FCSTD DOCUMENT  (FreeCAD 0.20R29410 (Git))
Label: simbologia-abnt
License: All rights reserved
objects: Part::Part2DObjectPython×43, App::FeaturePython×17, App::DocumentObjectGroup×12, Part::Mirroring×4, Part::FeaturePython×1
note: 47 computed .brp shape members not serialized (recipe doc carries the construction recipe); baked Part::Feature solids carry a one-line shape summary decoded from their .brp

FEATURE [Part::Part2DObjectPython] Line  # Draft 2D object (typed FeaturePython)
  Area = 0
  ChamferSize = 0
  Closed = true
  End = (0,7.75736,0)
  FilletRadius = 0
  Length = 7.75736
  MakeFace = true
  Points = (2) [(0,0,0),(0,7.75736,0)]
  Start = (0,0,0)
  Subdivisions = 0
FEATURE [Part::Part2DObjectPython] Line001  # Draft 2D object (typed FeaturePython)
  Area = 0
  ChamferSize = 0
  Closed = true
  End = (5,7.75736,0)
  FilletRadius = 0
  Length = 7.75736
  MakeFace = true
  Placement = pos=(5,0,0) rot=(0,0,1;0rad)
  Points = (2) [(0,0,0),(0,7.75736,0)]
  Start = (5,0,0)
  Subdivisions = 0
FEATURE [Part::Part2DObjectPython] Line003  # Draft 2D object (typed FeaturePython)
  Area = 0
  ChamferSize = 0
  Closed = false
  End = (6.74264,7.75736,0)
  FilletRadius = 0
  Length = 6
  MakeFace = true
  Placement = pos=(2.5,12,0) rot=(0,0,1;0.785398rad)
  Points = (2) [(0,0,0),(1.77636e-15,-6,0)]
  Start = (2.5,12,0)
  Subdivisions = 0
FEATURE [Part::Mirroring] mirror  label="Line003 (espelhado) "
  Base = (2.5,5.47945,0)
  Normal = (1,0,0)
  Source = -> Line003
FEATURE [Part::Part2DObjectPython] Line004  # Draft 2D object (typed FeaturePython)
  Area = 0
  ChamferSize = 0
  Closed = false
  End = (4e-16,7.75736,0)
  FilletRadius = 0
  Length = 1.74264
  MakeFace = true
  Placement = pos=(-1.74264,7.75736,0) rot=(0,0,1;0rad)
  Points = (2) [(0,0,0),(1.74264,0,0)]
  Start = (-1.74264,7.75736,0)
  Subdivisions = 0
FEATURE [Part::Part2DObjectPython] Line005  # Draft 2D object (typed FeaturePython)
  Area = 0
  ChamferSize = 0
  Closed = false
  End = (5,7.75736,0)
  FilletRadius = 0
  Length = 1.74264
  MakeFace = true
  Placement = pos=(6.74264,7.75736,0) rot=(0,0,1;0rad)
  Points = (2) [(0,0,0),(-1.74264,0,0)]
  Start = (6.74264,7.75736,0)
  Subdivisions = 0
FEATURE [Part::Part2DObjectPython] Line006  # Draft 2D object (typed FeaturePython)
  Area = 0
  ChamferSize = 0
  Closed = false
  End = (5,0,0)
  FilletRadius = 0
  Length = 5
  MakeFace = true
  Points = (2) [(0,0,0),(5,0,0)]
  Start = (0,0,0)
  Subdivisions = 0
FEATURE [App::FeaturePython] Text  label="ENTRADA"  # WARN: FeaturePython — macro-defined, semantics opaque (R4)
  Placement = pos=(-4.70483,-2.70715,0) rot=(0,0,1;0rad)
  Text = ENTRADA
FEATURE [App::DocumentObjectGroup] Group  label="simbologia-entrada"
  Group = -> [Line,Line001,mirror,Line004,Line005,Line006,Text]
FEATURE [Part::Part2DObjectPython] Line007  # Draft 2D object (typed FeaturePython)
  Area = 0
  ChamferSize = 0
  Closed = false
  End = (35.2588,-0.0306032,0)
  FilletRadius = 0
  Length = 12
  MakeFace = true
  Placement = pos=(23.2588,-0.0306032,0) rot=(0,0,1;0rad)
  Points = (2) [(0,0,0),(12,0,0)]
  Start = (23.2588,-0.0306032,0)
  Subdivisions = 0
FEATURE [Part::Part2DObjectPython] Line009  # Draft 2D object (typed FeaturePython)
  Area = 0
  ChamferSize = 0
  Closed = false
  End = (23.2588,-0.0306032,0)
  FilletRadius = 0
  Length = 8.48528
  MakeFace = true
  Placement = pos=(23.2588,-0.0306032,0) rot=(0,0,1;0.785398rad)
  Points = (2) [(7.10543e-15,-8.48528,0),(0,0,0)]
  Start = (29.2588,-6.0306,0)
  Subdivisions = 0
FEATURE [Part::Mirroring] mirror001  label="Line009 (espelhado) "
  Base = (29.2588,-0.0306032,0)
  Normal = (-1,0,0)
  Source = -> Line009
FEATURE [App::FeaturePython] Text001  label="INCLINAÇÃO"  # WARN: FeaturePython — macro-defined, semantics opaque (R4)
  Placement = pos=(26.5157,0.363858,0) rot=(0,0,1;0rad)
  Text = xx %
FEATURE [App::DocumentObjectGroup] Group001  label="simbologia-inclinação-telhado"
  Group = -> [Line007,mirror001,Text001]
FEATURE [Part::Part2DObjectPython] Circle  # Draft 2D object (typed FeaturePython)
  Area = 0
  FirstAngle = 0
  LastAngle = 0
  MakeFace = false
  Placement = pos=(46.9739,-0.162971,0) rot=(0,0,1;0rad)
  Radius = 6
FEATURE [Part::Part2DObjectPython] Line010  # Draft 2D object (typed FeaturePython)
  Area = 0
  ChamferSize = 0
  Closed = false
  End = (52.9739,-0.162971,0)
  FilletRadius = 0
  Length = 12
  MakeFace = true
  Placement = pos=(40.9739,-0.162971,0) rot=(0,0,1;0rad)
  Points = (2) [(0,0,0),(12,-7.21645e-16,0)]
  Start = (40.9739,-0.162971,0)
  Subdivisions = 0
FEATURE [Part::Part2DObjectPython] Line011  # Draft 2D object (typed FeaturePython)
  Area = 0
  ChamferSize = 0
  Closed = false
  End = (40.9739,-0.162971,0)
  FilletRadius = 0
  Length = 3
  MakeFace = true
  Placement = pos=(37.9739,-0.162971,0) rot=(0,0,1;0rad)
  Points = (2) [(0,0,0),(3,0,0)]
  Start = (37.9739,-0.162971,0)
  Subdivisions = 0
FEATURE [Part::Part2DObjectPython] Line013  # Draft 2D object (typed FeaturePython)
  Area = 0
  ChamferSize = 0
  Closed = false
  End = (55.9739,-0.162971,0)
  FilletRadius = 0
  Length = 3
  MakeFace = true
  Placement = pos=(52.9739,-0.162971,0) rot=(0,0,1;0rad)
  Points = (2) [(0,0,0),(3,0,0)]
  Start = (52.9739,-0.162971,0)
  Subdivisions = 0
FEATURE [Part::Part2DObjectPython] Line014  # Draft 2D object (typed FeaturePython)
  Area = 0
  ChamferSize = 0
  Closed = false
  End = (37.9739,-0.162971,0)
  FilletRadius = 0
  Length = 12.7279
  MakeFace = true
  Placement = pos=(37.9739,-0.162971,0) rot=(0,0,1;0rad)
  Points = (2) [(9,9,0),(0,-7.21645e-16,0)]
  Start = (46.9739,8.83703,0)
  Subdivisions = 0
FEATURE [Part::Mirroring] mirror002  label="Line014 (espelhado) "
  Base = (46.9739,13.4063,0)
  Normal = (-1,0,0)
  Source = -> Line014
FEATURE [App::FeaturePython] Text002  label="DESENHO-NUM"  # WARN: FeaturePython — macro-defined, semantics opaque (R4)
  Placement = pos=(45.2497,1.29047,0) rot=(0,0,1;0rad)
  Text = xx
FEATURE [App::FeaturePython] Text003  label="PRANCHA-NUM"  # WARN: FeaturePython — macro-defined, semantics opaque (R4)
  Placement = pos=(45.7357,-2.81605,0) rot=(0,0,1;0rad)
  Text = xx
FEATURE [App::DocumentObjectGroup] Group002  label="simbologia-elev-corte-fachada-vista"
  Group = -> [Circle,Line010,Line011,Line013,mirror002,Text002,Text003]
FEATURE [Part::Part2DObjectPython] Circle001  # Draft 2D object (typed FeaturePython)
  Area = 0
  FirstAngle = 0
  LastAngle = 0
  MakeFace = false
  Placement = pos=(72.2369,-0.0494289,0) rot=(0,0,1;0rad)
  Radius = 5
FEATURE [Part::Part2DObjectPython] Line017  # Draft 2D object (typed FeaturePython)
  Area = 0
  ChamferSize = 0
  Closed = false
  End = (92.2369,-0.0494289,0)
  FilletRadius = 0
  Length = 30
  MakeFace = true
  Placement = pos=(62.2369,-0.0494289,0) rot=(0,0,1;0rad)
  Points = (2) [(0,0,0),(30,0,0)]
  Start = (62.2369,-0.0494289,0)
  Subdivisions = 0
FEATURE [Part::Part2DObjectPython] Line018  # Draft 2D object (typed FeaturePython)
  Area = 0
  ChamferSize = 0
  Closed = false
  End = (71.9166,9.95057,0)
  FilletRadius = 0
  Length = 20
  MakeFace = true
  Placement = pos=(71.9166,-10.0494,0) rot=(0,0,1;0rad)
  Points = (2) [(0,0,0),(0,20,0)]
  Start = (71.9166,-10.0494,0)
  Subdivisions = 0
FEATURE [App::FeaturePython] Text004  label="NÍVEL-PLANTA"  # WARN: FeaturePython — macro-defined, semantics opaque (R4)
  Placement = pos=(77.4379,1.13189,0) rot=(0,0,1;0rad)
  Text = + XX,XX 
FEATURE [App::DocumentObjectGroup] Group003  label="simbologia-nível-planta"
  Group = -> [Circle001,Line017,Line018,Text004]
FEATURE [Part::Part2DObjectPython] Line019  # Draft 2D object (typed FeaturePython)
  Area = 0
  ChamferSize = 0
  Closed = false
  End = (111.872,1.47777,0)
  FilletRadius = 0
  Length = 2.5
  MakeFace = true
  Placement = pos=(113.64,-0.29,0) rot=(0,0,1;0.785398rad)
  Points = (2) [(0,0,0),(-1.42109e-14,2.5,0)]
  Start = (113.64,-0.29,0)
  Subdivisions = 0
FEATURE [Part::Mirroring] mirror003  label="Line019 (espelhado) "
  Base = (113.64,-0.29,0)
  Normal = (1,0,0)
  Source = -> Line019
FEATURE [Part::Part2DObjectPython] Line020  # Draft 2D object (typed FeaturePython)
  Area = 0
  ChamferSize = 0
  Closed = false
  End = (115.408,1.47777,0)
  FilletRadius = 0
  Length = 3.53553
  MakeFace = true
  Placement = pos=(111.872,1.47777,0) rot=(0,0,1;0rad)
  Points = (2) [(0,0,0),(3.53553,1.42109e-14,0)]
  Start = (111.872,1.47777,0)
  Subdivisions = 0
FEATURE [Part::Part2DObjectPython] Line021  # Draft 2D object (typed FeaturePython)
  Area = 0
  ChamferSize = 0
  Closed = false
  End = (115.408,1.47777,0)
  FilletRadius = 0
  Length = 3.53553
  MakeFace = true
  Placement = pos=(111.872,1.47777,0) rot=(0,0,1;0rad)
  Points = (2) [(0,0,0),(3.53553,1.42109e-14,0)]
  Start = (111.872,1.47777,0)
  Subdivisions = 0
FEATURE [Part::Part2DObjectPython] Line022  # Draft 2D object (typed FeaturePython)
  Area = 0
  ChamferSize = 0
  Closed = false
  End = (113.64,9.71,0)
  FilletRadius = 0
  Length = 10
  MakeFace = true
  Placement = pos=(113.64,-0.29,0) rot=(0,0,1;0rad)
  Points = (2) [(0,0,0),(0,10,0)]
  Start = (113.64,-0.29,0)
  Subdivisions = 0
FEATURE [App::FeaturePython] Text005  label="NÍVEL-CORTE"  # WARN: FeaturePython — macro-defined, semantics opaque (R4)
  Placement = pos=(114.511,5.46916,0) rot=(0,0,1;0rad)
  Text = + XX,XX  (X.X)
FEATURE [Part::Part2DObjectPython] Line026  # Draft 2D object (typed FeaturePython)
  Area = 0
  ChamferSize = 0
  Closed = false
  End = (131.687,4.71,0)
  FilletRadius = 0
  Length = 21.7968
  MakeFace = true
  Placement = pos=(109.89,4.71,0) rot=(0,0,1;0rad)
  Points = (2) [(0,0,0),(21.7968,0,0)]
  Start = (109.89,4.71,0)
  Subdivisions = 0
FEATURE [App::DocumentObjectGroup] Group004  label="simbologia-nível-corte"
  Group = -> [mirror003,Line020,Line021,Line022,Text005,Line026]
FEATURE [Part::Part2DObjectPython] Circle003  # Draft 2D object (typed FeaturePython)
  Area = 0
  FirstAngle = 0
  LastAngle = 0
  MakeFace = false
  Placement = pos=(190.551,-0.0194988,0) rot=(0,0,1;0rad)
  Radius = 6
FEATURE [Part::Part2DObjectPython] Line028  # Draft 2D object (typed FeaturePython)
  Area = 0
  ChamferSize = 0
  Closed = false
  End = (250,-0.02,0)
  FilletRadius = 0
  Length = 53.4486
  MakeFace = true
  Placement = pos=(196.551,-0.0194988,0) rot=(0,0,1;0rad)
  Points = (2) [(0,0,0),(53.4486,-0.000501236,0)]
  Start = (196.551,-0.0194988,0)
  Subdivisions = 0
FEATURE [App::FeaturePython] Text008  label="TITULO-DESENHO"  # WARN: FeaturePython — macro-defined, semantics opaque (R4)
  Placement = pos=(196.849,0.792427,0) rot=(0,0,1;0rad)
  Text = TITULO DO DESENHO
FEATURE [App::FeaturePython] Text009  label="NUM-DESENHO"  # WARN: FeaturePython — macro-defined, semantics opaque (R4)
  Placement = pos=(189.054,-1.69787,0) rot=(0,0,1;0rad)
  Text = X
FEATURE [App::FeaturePython] Text010  label="ESCALA-DESENHO"  # WARN: FeaturePython — macro-defined, semantics opaque (R4)
  Placement = pos=(196.849,-3.27118,0) rot=(0,0,1;0rad)
  Text = ESCALA
FEATURE [App::DocumentObjectGroup] Group006  label="simbologia-titulo-prancha"
  Group = -> [Circle003,Line028,Text008,Text009,Text010]
FEATURE [Part::Part2DObjectPython] Circle004  # Draft 2D object (typed FeaturePython)
  Area = 0
  FirstAngle = 0
  LastAngle = 0
  MakeFace = false
  Placement = pos=(273.103,0.232803,0) rot=(0,0,1;0rad)
  Radius = 3.5
FEATURE [App::FeaturePython] Text011  label="SIGLA-ESQUADRIAS"  # WARN: FeaturePython — macro-defined, semantics opaque (R4)
  Placement = pos=(271.713,-0.498117,0) rot=(0,0,1;0rad)
  Text = Xn
FEATURE [Part::Part2DObjectPython] Circle005  # Draft 2D object (typed FeaturePython)
  Area = 0
  FirstAngle = 0
  LastAngle = 0
  MakeFace = false
  Placement = pos=(273.418,11.7931,0) rot=(0,0,1;0rad)
  Radius = 3.5
FEATURE [App::FeaturePython] Text012  label="SIGLA-ESQUADRIAS001"  # WARN: FeaturePython — macro-defined, semantics opaque (R4)
  Placement = pos=(272.029,11.0621,0) rot=(0,0,1;0rad)
  Text = Xn
FEATURE [Part::Part2DObjectPython] Circle006  # Draft 2D object (typed FeaturePython)
  Area = 0
  FirstAngle = 0
  LastAngle = 0
  MakeFace = false
  Placement = pos=(273.418,23.0764,0) rot=(0,0,1;0rad)
  Radius = 3.5
FEATURE [App::FeaturePython] Text013  label="SIGLA-ESQUADRIAS002"  # WARN: FeaturePython — macro-defined, semantics opaque (R4)
  Placement = pos=(272.029,22.3455,0) rot=(0,0,1;0rad)
  Text = Xn
FEATURE [App::FeaturePython] Text014  label="LARGxALT"  # WARN: FeaturePython — macro-defined, semantics opaque (R4)
  Placement = pos=(277.408,23.7992,0) rot=(0,0,1;0rad)
  Text = X,X x X,X
FEATURE [App::FeaturePython] Text015  label="PEITORIL"  # WARN: FeaturePython — macro-defined, semantics opaque (R4)
  Placement = pos=(280.577,20.7534,0) rot=(0,0,1;0rad)
  Text = X,X
FEATURE [Part::Part2DObjectPython] Line031  # Draft 2D object (typed FeaturePython)
  Area = 0
  ChamferSize = 0
  Closed = false
  End = (288.532,23.0764,0)
  FilletRadius = 0
  Length = 11.6135
  MakeFace = true
  Placement = pos=(276.918,23.0764,0) rot=(0,0,1;0rad)
  Points = (2) [(0,0,0),(11.6135,0,0)]
  Start = (276.918,23.0764,0)
  Subdivisions = 0
FEATURE [Part::Part2DObjectPython] Line032  # Draft 2D object (typed FeaturePython)
  Area = 0
  ChamferSize = 0
  Closed = false
  End = (288.532,11.7931,0)
  FilletRadius = 0
  Length = 11.6135
  MakeFace = true
  Placement = pos=(276.918,11.7931,0) rot=(0,0,1;0rad)
  Points = (2) [(0,0,0),(11.6135,0,0)]
  Start = (276.918,11.7931,0)
  Subdivisions = 0
FEATURE [App::FeaturePython] Text016  label="LARGxALT001"  # WARN: FeaturePython — macro-defined, semantics opaque (R4)
  Placement = pos=(277.408,12.5158,0) rot=(0,0,1;0rad)
  Text = X,X x X,X
FEATURE [App::DocumentObjectGroup] Group007  label="simbologia-esquadrias-medidas"
  Group = -> [Circle004,Text011,Circle005,Text012,Circle006,Text013,Text014,Text015,Line031,Line032,Text016]
FEATURE [Part::Part2DObjectPython] Line027  # Draft 2D object (typed FeaturePython)
  Area = 0
  ChamferSize = 0
  Closed = false
  End = (169.147,0.17771,0)
  FilletRadius = 0
  Length = 12
  MakeFace = true
  Placement = pos=(157.147,0.17771,0) rot=(0,0,1;0rad)
  Points = (2) [(0,0,0),(12,-7.21645e-16,0)]
  Start = (157.147,0.17771,0)
  Subdivisions = 0
FEATURE [App::FeaturePython] Text007  label="DESENHO-NUM001"  # WARN: FeaturePython — macro-defined, semantics opaque (R4)
  Placement = pos=(161.423,1.61442,0) rot=(0,0,1;0rad)
  Text = xx
FEATURE [App::FeaturePython] Text006  label="PRANCHA-NUM001"  # WARN: FeaturePython — macro-defined, semantics opaque (R4)
  Placement = pos=(161.909,-2.4921,0) rot=(0,0,1;0rad)
  Text = xx
FEATURE [Part::Part2DObjectPython] Circle002  # Draft 2D object (typed FeaturePython)
  Area = 0
  FirstAngle = 0
  LastAngle = 0
  MakeFace = false
  Placement = pos=(163.147,0.17771,0) rot=(0,0,1;0rad)
  Radius = 6
FEATURE [App::DocumentObjectGroup] Group005  label="simbologia-detalhes-e-ampliações"
  Group = -> [Circle002,Text006,Text007,Line027]
FEATURE [Part::Part2DObjectPython] Rectangle  # Draft 2D object (typed FeaturePython)
  Area = 0
  ChamferSize = 0
  Columns = 1
  FilletRadius = 0
  Height = 5
  Length = 5
  MakeFace = false
  Placement = pos=(-0.647244,30.44,0) rot=(0,0,1;0rad)
  Rows = 1
FEATURE [Part::Part2DObjectPython] Line033  # Draft 2D object (typed FeaturePython)
  Area = 0
  ChamferSize = 0
  Closed = false
  End = (9.35276,30.44,0)
  FilletRadius = 0
  Length = 5
  MakeFace = true
  Placement = pos=(4.35276,30.44,0) rot=(0,0,1;0rad)
  Points = (2) [(0,0,0),(5,0,0)]
  Start = (4.35276,30.44,0)
  Subdivisions = 0
FEATURE [Part::Part2DObjectPython] Circle007  # Draft 2D object (typed FeaturePython)
  Area = 0
  FirstAngle = 0
  LastAngle = 0
  MakeFace = false
  Placement = pos=(11.9208,32.94,0) rot=(0,0,1;0rad)
  Radius = 3
FEATURE [Part::Part2DObjectPython] Wire  # Draft 2D object (typed FeaturePython)
  Area = 0
  ChamferSize = 0
  Closed = false
  End = (9.35276,30.44,0)
  FilletRadius = 0
  Length = 10.4193
  MakeFace = true
  Placement = pos=(4.35276,30.44,0) rot=(0,0,1;0rad)
  Points = (3) [(0,0,0),(2.5,4.5706,0),(5,0,0)]
  Start = (4.35276,30.44,0)
  Subdivisions = 0
FEATURE [App::DocumentObjectGroup] Group008  label="simbologia-revestimentos"
  Group = -> [Rectangle,Line033,Circle007,Wire]
FEATURE [Part::Part2DObjectPython] Rectangle001  # Draft 2D object (typed FeaturePython)
  Area = 0
  ChamferSize = 0
  Columns = 1
  FilletRadius = 0
  Height = 26.2006
  Length = 77.4526
  MakeFace = false
  Placement = pos=(304.633,0.159356,0) rot=(0,0,1;0rad)
  Rows = 1
FEATURE [Part::Part2DObjectPython] Line034  # Draft 2D object (typed FeaturePython)
  Area = 0
  ChamferSize = 0
  Closed = false
  End = (382.086,9.98457,0)
  FilletRadius = 0
  Length = 77.4526
  MakeFace = true
  Placement = pos=(304.633,9.98457,0) rot=(0,0,1;0rad)
  Points = (2) [(0,0,0),(77.4526,0,0)]
  Start = (304.633,9.98457,0)
  Subdivisions = 0
FEATURE [Part::Part2DObjectPython] Line036  # Draft 2D object (typed FeaturePython)
  Area = 0
  ChamferSize = 0
  Closed = false
  End = (382.086,19.8098,0)
  FilletRadius = 0
  Length = 77.4526
  MakeFace = true
  Placement = pos=(304.633,19.8098,0) rot=(0,0,1;0rad)
  Points = (2) [(0,0,0),(77.4526,0,0)]
  Start = (304.633,19.8098,0)
  Subdivisions = 0
FEATURE [Part::Part2DObjectPython] Line037  # Draft 2D object (typed FeaturePython)
  Area = 0
  ChamferSize = 0
  Closed = false
  End = (343.36,0.159356,0)
  FilletRadius = 0
  Length = 19.6504
  MakeFace = true
  Placement = pos=(343.36,19.8098,0) rot=(0,0,1;0rad)
  Points = (2) [(0,0,0),(0,-19.6504,0)]
  Start = (343.36,19.8098,0)
  Subdivisions = 0
FEATURE [Part::Part2DObjectPython] Line038  # Draft 2D object (typed FeaturePython)
  Area = 0
  ChamferSize = 0
  Closed = false
  End = (320,0.159574,0)
  FilletRadius = 0
  Length = 19.6504
  MakeFace = true
  Placement = pos=(320,19.81,0) rot=(0,0,1;0rad)
  Points = (2) [(0,0,0),(0,-19.6504,0)]
  Start = (320,19.81,0)
  Subdivisions = 0
FEATURE [App::DocumentObjectGroup] Group010  label="tb-esquadria"
  Group = -> [Rectangle001,Line034,Line036,Line037,Line038]
FEATURE [Part::Part2DObjectPython] Rectangle002  # Draft 2D object (typed FeaturePython)
  Area = 0
  ChamferSize = 0
  Columns = 1
  FilletRadius = 0
  Height = 26.2006
  Length = 77.4526
  MakeFace = false
  Placement = pos=(400,0.16,0) rot=(0,0,1;0rad)
  Rows = 1
FEATURE [Part::Part2DObjectPython] Line039  # Draft 2D object (typed FeaturePython)
  Area = 0
  ChamferSize = 0
  Closed = false
  End = (430,0.159431,0)
  FilletRadius = 0
  Length = 26.2006
  MakeFace = true
  Placement = pos=(430,26.36,0) rot=(0,0,1;0rad)
  Points = (2) [(0,0,0),(0,-26.2006,0)]
  Start = (430,26.36,0)
  Subdivisions = 0
FEATURE [Part::FeaturePython] Array  # Draft array (typed FeaturePython)
  AlwaysSyncPlacement = false
  Angle = 360
  ArrayType = 0
  Axis = (0,0,1)
  Base = -> Line039
  Center = (0,0,0)
  Count = 6
  ExpandArray = false
  Fuse = false
  IntervalAxis = (0,0,0)
  IntervalX = (16,0,0)
  IntervalY = (0,0,0)
  IntervalZ = (0,0,0)
  NumberCircles = 3
  NumberPolar = 5
  NumberX = 3
  NumberY = 2
  NumberZ = 1
  PlacementList = 6 placements: [(430,26.36,0),(430,26.36,0),(446,26.36,0),(446,26.36,0),(462,26.36,0),(462,26.36,0)]
  RadialDistance = 50
  ScaleList = (6) [(1,1,1),(1,1,1),(1,1,1),(1,1,1),(1,1,1),(1,1,1)]
  Symmetry = 1
  TangentialDistance = 25
FEATURE [Part::Part2DObjectPython] Line040  # Draft 2D object (typed FeaturePython)
  Area = 0
  ChamferSize = 0
  Closed = false
  End = (477.453,13.16,0)
  FilletRadius = 0
  Length = 77.4526
  MakeFace = true
  Placement = pos=(400,13.16,0) rot=(0,0,1;0rad)
  Points = (2) [(0,0,0),(77.4526,0,0)]
  Start = (400,13.16,0)
  Subdivisions = 0
FEATURE [Part::Part2DObjectPython] Line041  # Draft 2D object (typed FeaturePython)
  Area = 0
  ChamferSize = 0
  Closed = false
  End = (430,13.2597,0)
  FilletRadius = 0
  Length = 32.7358
  MakeFace = true
  Placement = pos=(400,26.3606,0) rot=(0,0,1;0rad)
  Points = (2) [(0,0,0),(30,-13.1009,0)]
  Start = (400,26.3606,0)
  Subdivisions = 0
FEATURE [App::DocumentObjectGroup] Group011  label="tb-materiais"
  Group = -> [Rectangle002,Array,Line040,Line041]
FEATURE [App::DocumentObjectGroup] Group009  label="tabelas"
  Group = -> [Group010,Group011]
